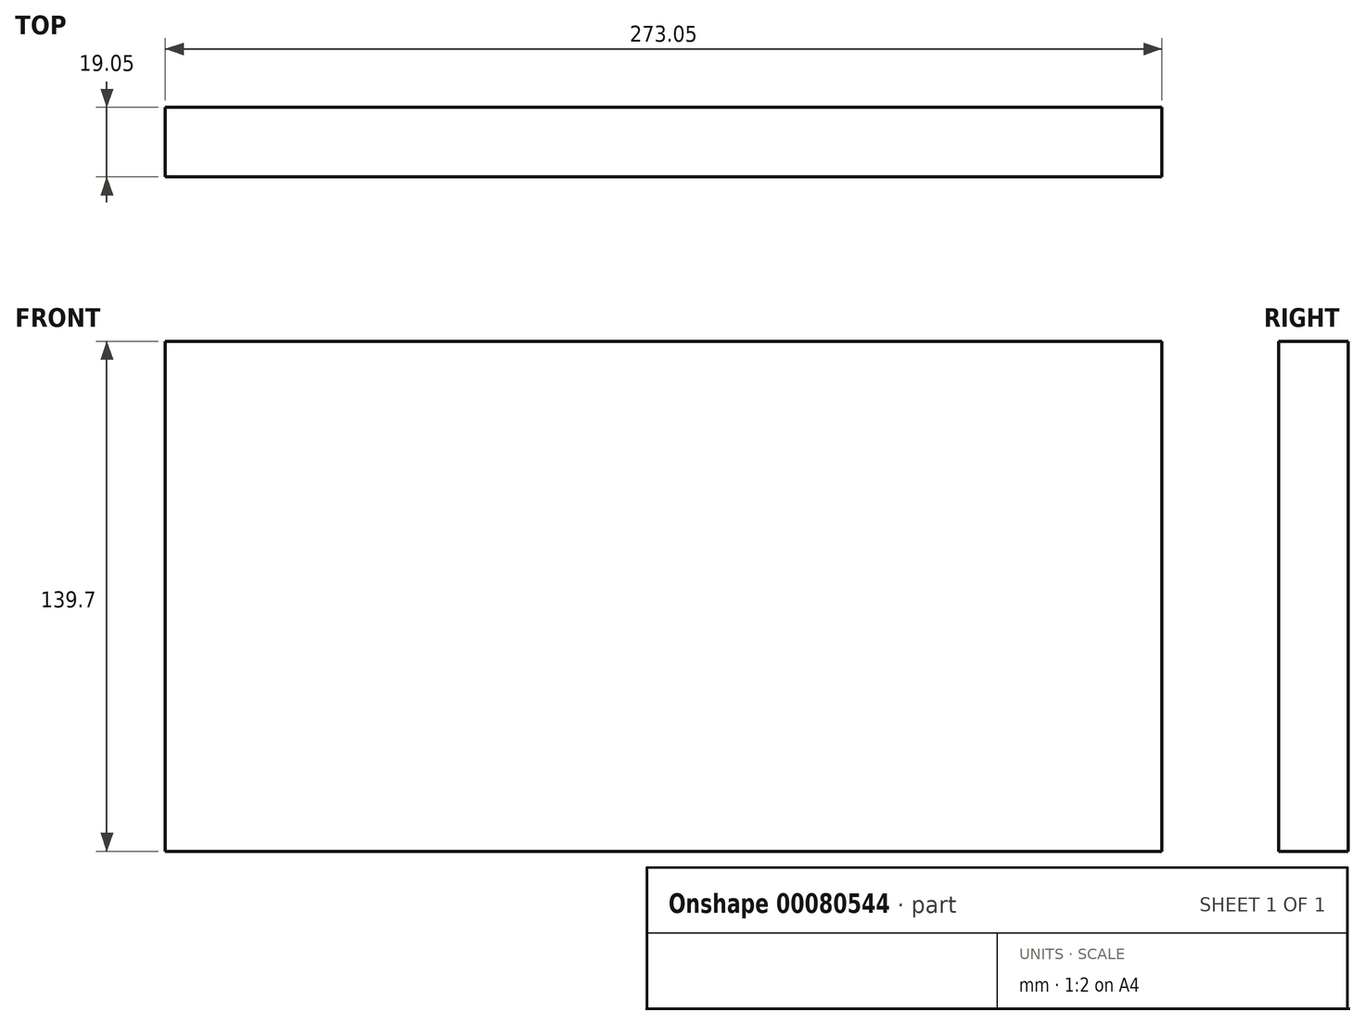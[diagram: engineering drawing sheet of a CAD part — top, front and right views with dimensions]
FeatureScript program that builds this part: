
annotation { "Feature Type Name" : "Feature", "Feature Type Description" : "" }
export const myFeature = defineFeature(function(context is Context, id is Id, definition is map)
    precondition{}
    {
        {
            var Q0;
            Q0=qCreatedBy(makeId("Front.planeOp"),FACE);
            var sketch = newSketch(context, id + "F0", { "sketchPlane" : qUnion([Q0])});
            skLineSegment(sketch, "E0.bottom", {"start": v(-174.35, 0) * mm, "end": v(-447.4, 0) * mm});
            skLineSegment(sketch, "E0.top", {"start": v(-174.35, 139.7) * mm, "end": v(-447.4, 139.7) * mm});
            skLineSegment(sketch, "E0.left", {"start": v(-174.35, 0) * mm, "end": v(-174.35, 139.7) * mm});
            skLineSegment(sketch, "E0.right", {"start": v(-447.4, 0) * mm, "end": v(-447.4, 139.7) * mm});
            skSolve(sketch);
        }
        {
            var Q0;
            Q0=makeQuery(id+"F0.imprint","IMPRINT",FACE,{"disambiguationData":[TD([[makeQuery(id+"F0.imprint","IMPRINT",EDGE,{"derivedFrom":sQuery(id+"F0.wireOp",EDGE,"E0.bottom")}),-1.0]])]});
            extrude(context, id + "F1", {"entities" : qUnion([Q0]), "depth" : 19.05 * mm});
        }
    });
